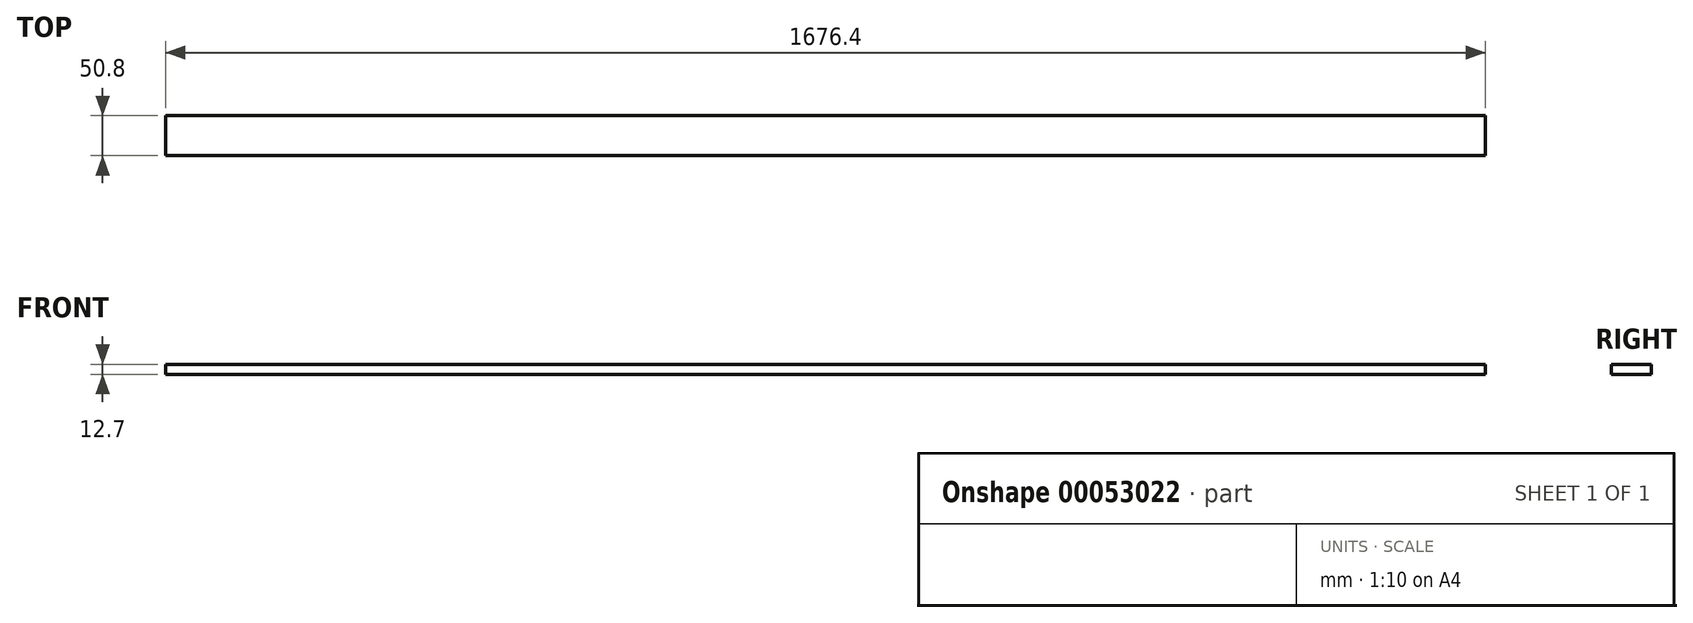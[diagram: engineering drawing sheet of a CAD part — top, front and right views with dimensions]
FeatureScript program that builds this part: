
annotation { "Feature Type Name" : "Feature", "Feature Type Description" : "" }
export const myFeature = defineFeature(function(context is Context, id is Id, definition is map)
    precondition{}
    {
        {
            var Q0;
            Q0=qCreatedBy(makeId("Right.planeOp"),FACE);
            var sketch = newSketch(context, id + "F0", { "sketchPlane" : qUnion([Q0])});
            skLineSegment(sketch, "E0.bottom", {"start": v(0, 0) * mm, "end": v(-50.8, 0) * mm});
            skLineSegment(sketch, "E0.top", {"start": v(0, 12.7) * mm, "end": v(-50.8, 12.7) * mm});
            skLineSegment(sketch, "E0.left", {"start": v(0, 0) * mm, "end": v(0, 12.7) * mm});
            skLineSegment(sketch, "E0.right", {"start": v(-50.8, 0) * mm, "end": v(-50.8, 12.7) * mm});
            skSolve(sketch);
        }
        {
            var Q0;
            Q0=makeQuery(id+"F0.imprint","IMPRINT",FACE,{"disambiguationData":[TD([[makeQuery(id+"F0.imprint","IMPRINT",EDGE,{"derivedFrom":sQuery(id+"F0.wireOp",EDGE,"E0.bottom")}),-1.0]])]});
            extrude(context, id + "F1", {"entities" : qUnion([Q0]), "depth" : 1676.4 * mm});
        }
    });
